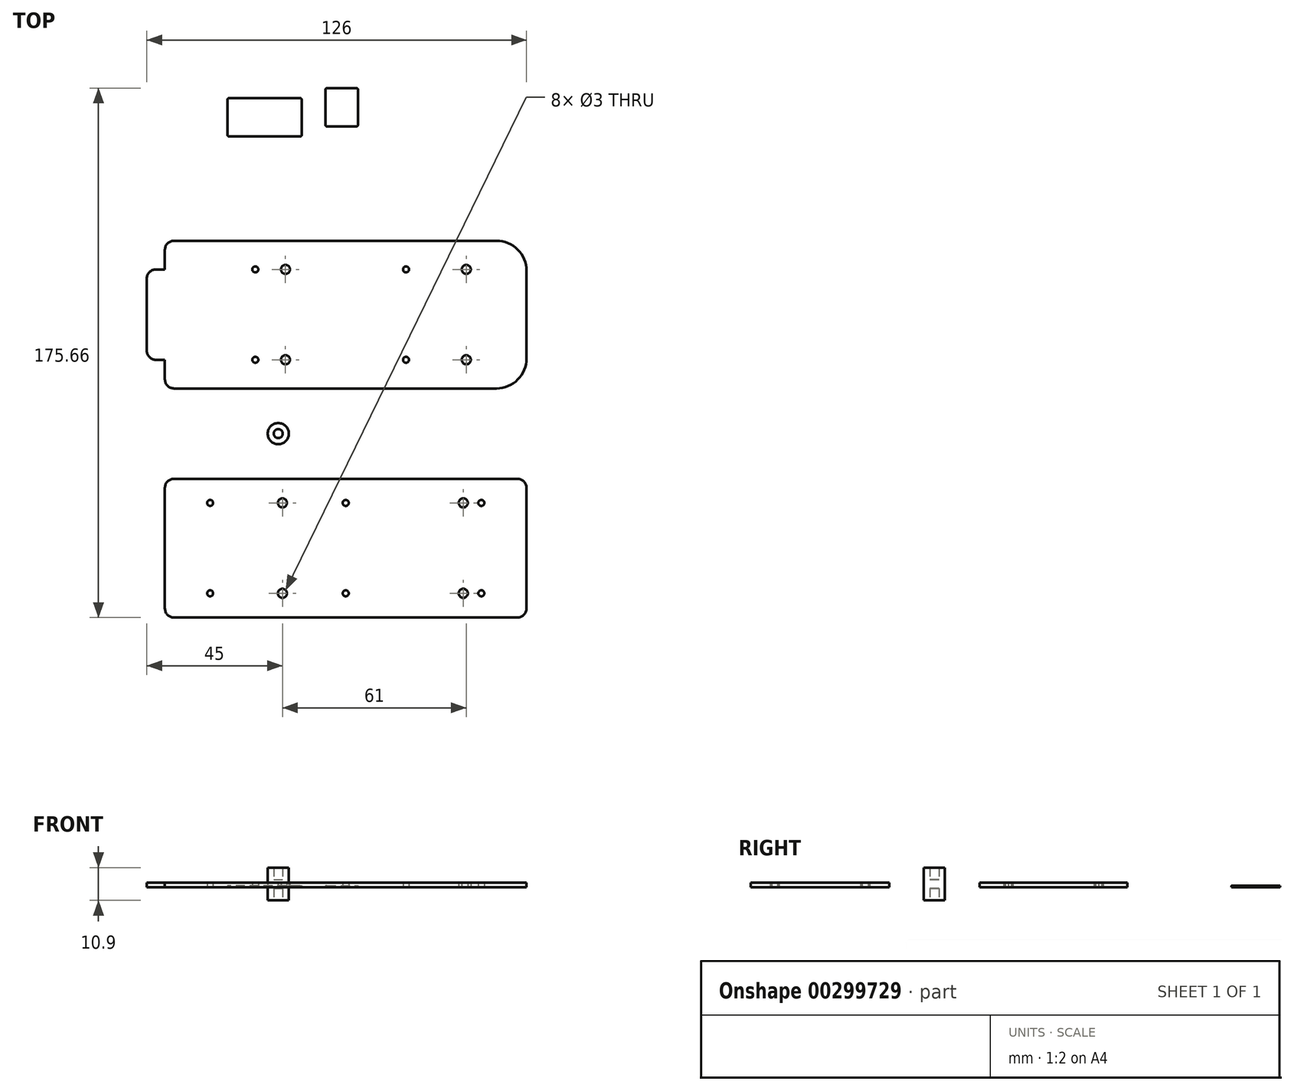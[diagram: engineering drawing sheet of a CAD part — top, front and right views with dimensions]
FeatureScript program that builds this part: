
annotation { "Feature Type Name" : "Feature", "Feature Type Description" : "" }
export const myFeature = defineFeature(function(context is Context, id is Id, definition is map)
    precondition{}
    {
        {
            var Q0;
            Q0=qCreatedBy(makeId("Top.planeOp"),FACE);
            var sketch = newSketch(context, id + "F0", { "sketchPlane" : qUnion([Q0])});
            skLineSegment(sketch, "E0.bottom", {"start": v(57, -15) * mm, "end": v(-57, -15) * mm});
            skLineSegment(sketch, "E0.top", {"start": v(57, -61) * mm, "end": v(-57, -61) * mm});
            skLineSegment(sketch, "E0.left", {"start": v(60, -18) * mm, "end": v(60, -58) * mm});
            skLineSegment(sketch, "E0.right", {"start": v(-60, -18) * mm, "end": v(-60, -58) * mm});
            skLineSegment(sketch, "E1.bottom", {"start": v(-57, 64) * mm, "end": v(50, 64) * mm});
            skLineSegment(sketch, "E1.top", {"start": v(-57, 15) * mm, "end": v(50, 15) * mm});
            skLineSegment(sketch, "E1.left", {"start": v(-60, 61) * mm, "end": v(-60, 54.5) * mm});
            skLineSegment(sketch, "E1.right", {"start": v(60, 54) * mm, "end": v(60, 25) * mm});
            skLineSegment(sketch, "E2", {"start": v(0, 15) * mm, "end": v(0, -15) * mm, "construction": true});
            skPoint(sketch, "E3.visualSharp", {"position": v(-60, 15) * mm});
            skArc(sketch, "E3.filletArc", {"start": v(-60, 18) * mm, "mid": v(-59.12, 15.88) * mm, "end": v(-57, 15) * mm});
            skPoint(sketch, "E4.visualSharp", {"position": v(-60, 64) * mm});
            skArc(sketch, "E4.filletArc", {"start": v(-57, 64) * mm, "mid": v(-59.12, 63.12) * mm, "end": v(-60, 61) * mm});
            skPoint(sketch, "E5.visualSharp", {"position": v(60, 64) * mm});
            skArc(sketch, "E5.filletArc", {"start": v(60, 54) * mm, "mid": v(57.07, 61.07) * mm, "end": v(50, 64) * mm});
            skPoint(sketch, "E6.visualSharp", {"position": v(60, 15) * mm});
            skArc(sketch, "E6.filletArc", {"start": v(50, 15) * mm, "mid": v(57.07, 17.93) * mm, "end": v(60, 25) * mm});
            skPoint(sketch, "E7.visualSharp", {"position": v(60, -15) * mm});
            skArc(sketch, "E7.filletArc", {"start": v(60, -18) * mm, "mid": v(59.12, -15.88) * mm, "end": v(57, -15) * mm});
            skPoint(sketch, "E8.visualSharp", {"position": v(-60, -15) * mm});
            skArc(sketch, "E8.filletArc", {"start": v(-57, -15) * mm, "mid": v(-59.12, -15.88) * mm, "end": v(-60, -18) * mm});
            skPoint(sketch, "E9.visualSharp", {"position": v(-60, -61) * mm});
            skArc(sketch, "E9.filletArc", {"start": v(-60, -58) * mm, "mid": v(-59.12, -60.12) * mm, "end": v(-57, -61) * mm});
            skPoint(sketch, "E10.visualSharp", {"position": v(60, -61) * mm});
            skArc(sketch, "E10.filletArc", {"start": v(57, -61) * mm, "mid": v(59.12, -60.12) * mm, "end": v(60, -58) * mm});
            skCircle(sketch, "E11", {"center": v(39, -23) * mm, "radius": 1.5 * mm});
            skCircle(sketch, "E12", {"center": v(39, -53) * mm, "radius": 1.5 * mm});
            skCircle(sketch, "E13", {"center": v(-21, -53) * mm, "radius": 1.5 * mm});
            skCircle(sketch, "E14", {"center": v(-21, -23) * mm, "radius": 1.5 * mm});
            skLineSegment(sketch, "E15", {"start": v(-21, -53) * mm, "end": v(-21, -23) * mm, "construction": true});
            skLineSegment(sketch, "E16", {"start": v(-21, -38) * mm, "end": v(-60, -38) * mm, "construction": true});
            skCircle(sketch, "E17", {"center": v(-20, 54.5) * mm, "radius": 1.5 * mm});
            skLineSegment(sketch, "E18", {"start": v(-60, 39.5) * mm, "end": v(60, 39.5) * mm, "construction": true});
            skCircle(sketch, "E19.MirrorC", {"center": v(40, 54.5) * mm, "radius": 1.5 * mm});
            skCircle(sketch, "E20.MirrorC", {"center": v(-20, 24.5) * mm, "radius": 1.5 * mm});
            skCircle(sketch, "E21.MirrorC", {"center": v(40, 24.5) * mm, "radius": 1.5 * mm});
            skLineSegment(sketch, "E22", {"start": v(-60, 24.5) * mm, "end": v(-63, 24.5) * mm});
            skLineSegment(sketch, "E23", {"start": v(-66, 27.5) * mm, "end": v(-66, 51.5) * mm});
            skLineSegment(sketch, "E24", {"start": v(-63, 54.5) * mm, "end": v(-60, 54.5) * mm});
            skLineSegment(sketch, "E25.trimOffspring", {"start": v(-60, 24.5) * mm, "end": v(-60, 18) * mm});
            skPoint(sketch, "E26.visualSharp", {"position": v(-66, 24.5) * mm});
            skArc(sketch, "E26.filletArc", {"start": v(-66, 27.5) * mm, "mid": v(-65.12, 25.38) * mm, "end": v(-63, 24.5) * mm});
            skPoint(sketch, "E27.visualSharp", {"position": v(-66, 54.5) * mm});
            skArc(sketch, "E27.filletArc", {"start": v(-63, 54.5) * mm, "mid": v(-65.12, 53.62) * mm, "end": v(-66, 51.5) * mm});
            skCircle(sketch, "E28", {"center": v(-30, 24.5) * mm, "radius": 1 * mm});
            skCircle(sketch, "E29", {"center": v(20, 24.5) * mm, "radius": 1 * mm});
            skCircle(sketch, "E30.MirrorC", {"center": v(20, 54.5) * mm, "radius": 1 * mm});
            skCircle(sketch, "E31.MirrorC", {"center": v(-30, 54.5) * mm, "radius": 1 * mm});
            skCircle(sketch, "E32", {"center": v(-45, -23) * mm, "radius": 1 * mm});
            skCircle(sketch, "E33.0.1.0", {"center": v(-45, -53) * mm, "radius": 1 * mm});
            skCircle(sketch, "E33.1.0.0", {"center": v(0, -23) * mm, "radius": 1 * mm});
            skCircle(sketch, "E33.1.1.0", {"center": v(0, -53) * mm, "radius": 1 * mm});
            skCircle(sketch, "E33.2.0.0", {"center": v(45, -23) * mm, "radius": 1 * mm});
            skCircle(sketch, "E33.2.1.0", {"center": v(45, -53) * mm, "radius": 1 * mm});
            skLineSegment(sketch, "E33.direction1", {"start": v(-45, -23) * mm, "end": v(0, -23) * mm, "construction": true});
            skLineSegment(sketch, "E33.direction2", {"start": v(-45, -23) * mm, "end": v(-45, -53) * mm, "construction": true});
            skSolve(sketch);
        }
        {
            var Q0;
            Q0=makeQuery(id+"F0.imprint","IMPRINT",FACE,{"disambiguationData":[TD([[makeQuery(id+"F0.imprint","IMPRINT",EDGE,{"derivedFrom":sQuery(id+"F0.wireOp",EDGE,"E1.bottom")}),-1.0]])]});
            extrude(context, id + "F1", {"entities" : qUnion([Q0]), "depth" : 1.5 * mm});
        }
        {
            var Q0;
            Q0=makeQuery(id+"F0.imprint","IMPRINT",FACE,{"disambiguationData":[TD([[makeQuery(id+"F0.imprint","IMPRINT",EDGE,{"derivedFrom":sQuery(id+"F0.wireOp",EDGE,"E0.bottom")}),1.0]])]});
            extrude(context, id + "F2", {"entities" : qUnion([Q0]), "depth" : 1.5 * mm});
        }
        {
            var Q0;
            Q0=qCreatedBy(makeId("Front.planeOp"),FACE);
            var sketch = newSketch(context, id + "F3", { "sketchPlane" : qUnion([Q0])});
            skLineSegment(sketch, "E34", {"start": v(-22.39, 2.52) * mm, "end": v(-20.89, 2.52) * mm});
            skLineSegment(sketch, "E35", {"start": v(-20.89, 2.52) * mm, "end": v(-20.89, 6.52) * mm});
            skLineSegment(sketch, "E36", {"start": v(-20.89, 6.52) * mm, "end": v(-18.89, 6.52) * mm});
            skLineSegment(sketch, "E37", {"start": v(-18.89, 6.52) * mm, "end": v(-18.89, -4.38) * mm});
            skLineSegment(sketch, "E38", {"start": v(-18.89, -4.38) * mm, "end": v(-20.89, -4.38) * mm});
            skLineSegment(sketch, "E39", {"start": v(-20.89, -4.38) * mm, "end": v(-20.89, -0.38) * mm});
            skLineSegment(sketch, "E40", {"start": v(-20.89, -0.38) * mm, "end": v(-22.39, -0.38) * mm});
            skLineSegment(sketch, "E41", {"start": v(-22.39, -0.38) * mm, "end": v(-22.39, 2.52) * mm});
            skPoint(sketch, "E42.orphan", {"position": v(-23.89, 2.52) * mm});
            skPoint(sketch, "E43.orphan", {"position": v(-23.89, -0.38) * mm});
            skSolve(sketch);
        }
        {
            var Q0;
            Q0=makeQuery(id+"F3.imprint","IMPRINT",FACE,{"disambiguationData":[TD([[makeQuery(id+"F3.imprint","IMPRINT",EDGE,{"derivedFrom":sQuery(id+"F3.wireOp",EDGE,"E34")}),-1.0]])]});
            var Q1;
            Q1=sQuery(id+"F3.wireOp",EDGE,"E34");
            var Q2;
            Q2=sQuery(id+"F3.wireOp",EDGE,"E35");
            var Q3;
            Q3=sQuery(id+"F3.wireOp",EDGE,"E36");
            var Q4;
            Q4=sQuery(id+"F3.wireOp",EDGE,"E37");
            var Q5;
            Q5=sQuery(id+"F3.wireOp",EDGE,"E38");
            var Q6;
            Q6=sQuery(id+"F3.wireOp",EDGE,"E39");
            var Q7;
            Q7=sQuery(id+"F3.wireOp",EDGE,"E41");
            var Q8;
            Q8=sQuery(id+"F3.wireOp",EDGE,"E41");
            revolve(context, id + "F4", {"entities" : qUnion([Q0]), "surfaceEntities" : qUnion([Q1, Q2, Q3, Q4, Q5, Q6, Q7]), "axis" : qUnion([Q8]), "revolveType" : RevolveType.FULL});
        }
        {
            var Q0;
            Q0=qCreatedBy(makeId("Top.planeOp"),FACE);
            var sketch = newSketch(context, id + "F5", { "sketchPlane" : qUnion([Q0])});
            skLineSegment(sketch, "E44.bottom", {"start": v(-6.24, 114.66) * mm, "end": v(3.56, 114.66) * mm});
            skLineSegment(sketch, "E44.top", {"start": v(-6.24, 101.96) * mm, "end": v(3.56, 101.96) * mm});
            skLineSegment(sketch, "E44.left", {"start": v(-6.74, 114.16) * mm, "end": v(-6.74, 102.46) * mm});
            skLineSegment(sketch, "E44.right", {"start": v(4.06, 114.16) * mm, "end": v(4.06, 102.46) * mm});
            skLineSegment(sketch, "E45.bottom", {"start": v(-15.1, 111.32) * mm, "end": v(-38.74, 111.32) * mm});
            skLineSegment(sketch, "E45.top", {"start": v(-15.1, 98.62) * mm, "end": v(-38.74, 98.62) * mm});
            skLineSegment(sketch, "E45.left", {"start": v(-14.6, 110.82) * mm, "end": v(-14.6, 99.12) * mm});
            skLineSegment(sketch, "E45.right", {"start": v(-39.24, 110.82) * mm, "end": v(-39.24, 99.12) * mm});
            skPoint(sketch, "E46.visualSharp", {"position": v(-39.24, 111.32) * mm});
            skArc(sketch, "E46.filletArc", {"start": v(-38.74, 111.32) * mm, "mid": v(-39.1, 111.17) * mm, "end": v(-39.24, 110.82) * mm});
            skPoint(sketch, "E47.visualSharp", {"position": v(-39.24, 98.62) * mm});
            skArc(sketch, "E47.filletArc", {"start": v(-39.24, 99.12) * mm, "mid": v(-39.1, 98.76) * mm, "end": v(-38.74, 98.62) * mm});
            skPoint(sketch, "E48.visualSharp", {"position": v(-14.6, 111.32) * mm});
            skArc(sketch, "E48.filletArc", {"start": v(-14.6, 110.82) * mm, "mid": v(-14.74, 111.17) * mm, "end": v(-15.1, 111.32) * mm});
            skPoint(sketch, "E49.visualSharp", {"position": v(-14.6, 98.62) * mm});
            skArc(sketch, "E49.filletArc", {"start": v(-15.1, 98.62) * mm, "mid": v(-14.74, 98.76) * mm, "end": v(-14.6, 99.12) * mm});
            skPoint(sketch, "E50.visualSharp", {"position": v(-6.74, 101.96) * mm});
            skArc(sketch, "E50.filletArc", {"start": v(-6.74, 102.46) * mm, "mid": v(-6.6, 102.1) * mm, "end": v(-6.24, 101.96) * mm});
            skPoint(sketch, "E51.visualSharp", {"position": v(-6.74, 114.66) * mm});
            skArc(sketch, "E51.filletArc", {"start": v(-6.24, 114.66) * mm, "mid": v(-6.6, 114.51) * mm, "end": v(-6.74, 114.16) * mm});
            skPoint(sketch, "E52.visualSharp", {"position": v(4.06, 114.66) * mm});
            skArc(sketch, "E52.filletArc", {"start": v(4.06, 114.16) * mm, "mid": v(3.92, 114.51) * mm, "end": v(3.56, 114.66) * mm});
            skPoint(sketch, "E53.visualSharp", {"position": v(4.06, 101.96) * mm});
            skArc(sketch, "E53.filletArc", {"start": v(3.56, 101.96) * mm, "mid": v(3.92, 102.1) * mm, "end": v(4.06, 102.46) * mm});
            skSolve(sketch);
        }
        {
            var Q0;
            Q0=makeQuery(id+"F5.imprint","IMPRINT",FACE,{"disambiguationData":[TD([[makeQuery(id+"F5.imprint","IMPRINT",EDGE,{"derivedFrom":sQuery(id+"F5.wireOp",EDGE,"E45.bottom")}),1.0]])]});
            var Q1;
            Q1=makeQuery(id+"F5.imprint","IMPRINT",FACE,{"disambiguationData":[TD([[makeQuery(id+"F5.imprint","IMPRINT",EDGE,{"derivedFrom":sQuery(id+"F5.wireOp",EDGE,"E44.bottom")}),-1.0]])]});
            extrude(context, id + "F6", {"entities" : qUnion([Q0, Q1]), "depth" : 0.5 * mm});
        }
    });
